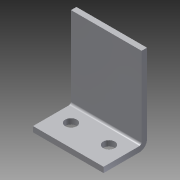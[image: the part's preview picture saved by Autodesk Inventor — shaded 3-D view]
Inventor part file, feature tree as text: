
AUTODESK INVENTOR PART (.ipt)
format: ipt  version: 2013 (Build 170138000, 138)  size: 104,448 bytes
history: native  units: in
note: dims shown in document units (in); Inventor stores cm internally (conversion verified against a paired STEP export)
features: sheet_metal_op x4, sketch x2, other x2
ambient origin geometry x8: Origin, YZ Plane, XZ Plane, XY Plane, X Axis, Y Axis, Z Axis, Center Point
bodies: Solid1 (feature_tree)
feature tree (8):
  sheet_metal_op  "Face1"
  sheet_metal_op  "Flange1"
  sketch  "Sketch1"  dims[d0=1.0in]
  other  "Plate1"
  sketch  "Sketch2"  dims[d2=0.266in d3=0.266in d4=0.875in d5=0.375in d6=0.375in d7=0.5in d8=0.5in d9=0.125in d10=0.125in d11=0.0625in d12=0.25in d13=0.125in d14=2.0in d15=90.0deg d16=0.05in d17=0.5in d18=0.125in d19=0.125in]
  other  "Plate2"
  sheet_metal_op  "Bend1"
  sheet_metal_op  "Corner1"
